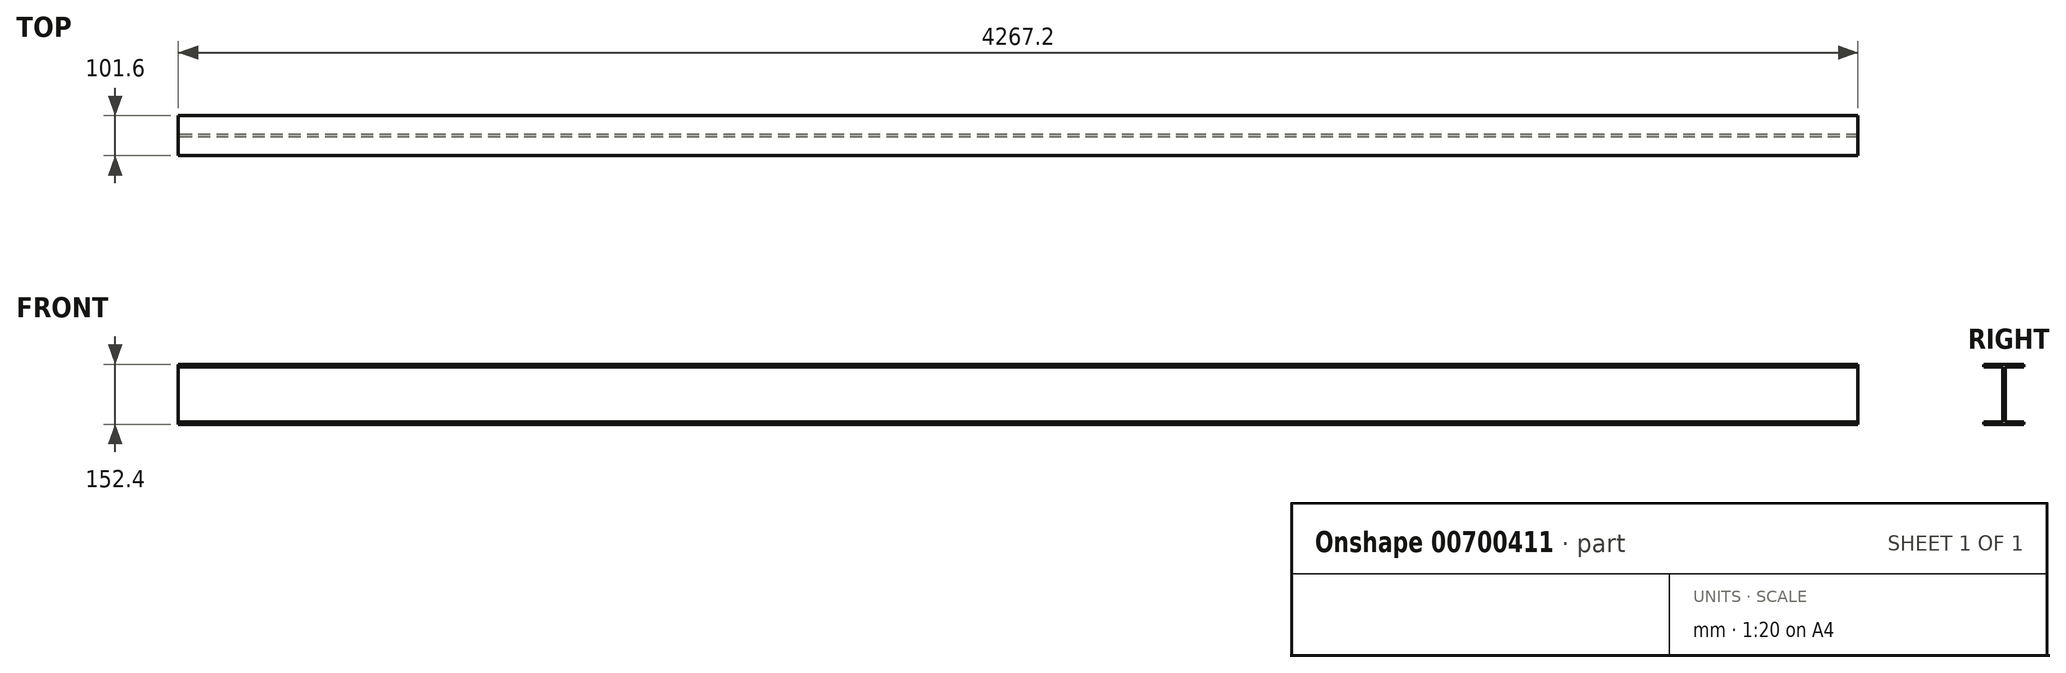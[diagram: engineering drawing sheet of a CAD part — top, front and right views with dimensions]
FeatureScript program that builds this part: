
annotation { "Feature Type Name" : "Feature", "Feature Type Description" : "" }
export const myFeature = defineFeature(function(context is Context, id is Id, definition is map)
    precondition{}
    {
        {
            var Q0;
            Q0=qCreatedBy(makeId("Right.planeOp"),FACE);
            var sketch = newSketch(context, id + "F0", { "sketchPlane" : qUnion([Q0])});
            skLineSegment(sketch, "E0", {"start": v(-50.8, 76.2) * mm, "end": v(50.8, 76.2) * mm});
            skLineSegment(sketch, "E1", {"start": v(50.8, 76.2) * mm, "end": v(50.8, 69.85) * mm});
            skLineSegment(sketch, "E2", {"start": v(50.8, 69.85) * mm, "end": v(3.17, 69.85) * mm});
            skLineSegment(sketch, "E3", {"start": v(3.17, 69.85) * mm, "end": v(3.18, -69.85) * mm});
            skLineSegment(sketch, "E4", {"start": v(3.18, -69.85) * mm, "end": v(50.8, -69.85) * mm});
            skLineSegment(sketch, "E5", {"start": v(-50.8, 76.2) * mm, "end": v(-50.8, 69.85) * mm});
            skLineSegment(sketch, "E6", {"start": v(-50.8, 69.85) * mm, "end": v(-3.18, 69.85) * mm});
            skLineSegment(sketch, "E7", {"start": v(-3.18, 69.85) * mm, "end": v(-3.17, -69.85) * mm});
            skLineSegment(sketch, "E8", {"start": v(-3.17, -69.85) * mm, "end": v(-50.8, -69.85) * mm});
            skLineSegment(sketch, "E9", {"start": v(-50.8, -69.85) * mm, "end": v(-50.8, -76.2) * mm});
            skLineSegment(sketch, "E10", {"start": v(-50.8, -76.2) * mm, "end": v(50.8, -76.2) * mm});
            skLineSegment(sketch, "E11", {"start": v(50.8, -76.2) * mm, "end": v(50.8, -69.85) * mm});
            skLineSegment(sketch, "E12", {"start": v(3.17, 69.85) * mm, "end": v(-3.17, -69.85) * mm, "construction": true});
            skSolve(sketch);
        }
        {
            var Q0;
            Q0 = qSketchRegion(id + "F0", true);
            extrude(context, id + "F1", {"entities" : qUnion([Q0]), "depth" : 4267.2 * mm, "offsetDistance" : 25.4 * mm});
        }
    });
